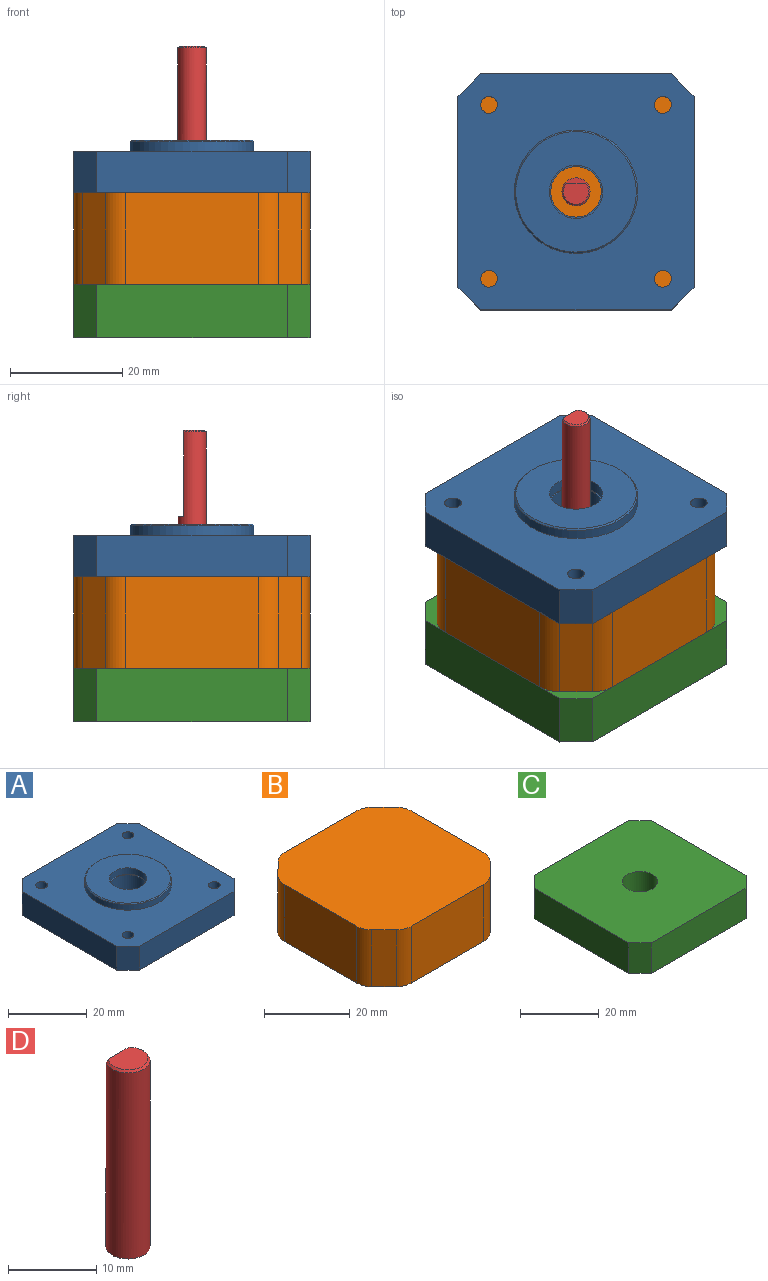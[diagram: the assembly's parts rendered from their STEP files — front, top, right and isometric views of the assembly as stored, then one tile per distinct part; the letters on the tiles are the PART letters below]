
ASSEMBLY  parts=4 mates=3
PART A: 20 faces, bbox 42.1x42.1x9.4 mm
  f0: plane 9.5x9.5mm, normal (0,0,1), area 7.3mm2, adj f11,f16
  f1: plane 34x7.4mm, normal (0,1,0), area 251.6mm2, adj f2,f12,f14,f15
  f2: plane 7.4x4.05mm, normal (-0.71,0.71,0), area 42.4mm2, adj f1,f3,f14,f15
  f3: plane 34x7.4mm, normal (-1,0,0), area 251.6mm2, adj f2,f4,f14,f15
  f4: plane 7.4x4.05mm, normal (-0.71,-0.71,0), area 42.4mm2, adj f3,f5,f14,f15
  f5: plane 34x7.4mm, normal (0,-1,0), area 251.6mm2, adj f4,f6,f14,f15
  f6: plane 7.4x4.05mm, normal (0.71,-0.71,0), area 42.4mm2, adj f5,f7,f14,f15
  f7: plane 34x7.4mm, normal (1,0,0), area 251.6mm2, adj f6,f12,f14,f15
  f8: cylinder r=1.5mm len=7.4mm, axis (0,0,-1), area 69.7mm2, adj f14,f15
  f9: cylinder r=1.5mm len=7.4mm, axis (0,0,-1), area 69.7mm2, adj f14,f15
  f10: cylinder r=1.5mm len=7.4mm, axis (0,0,-1), area 69.7mm2, adj f14,f15
  f11: cylinder r=4.5mm len=9mm, axis (0,0,-1), area 209.2mm2, adj f0,f15
  f12: plane 7.4x4.05mm, normal (0.71,0.71,0), area 42.4mm2, adj f1,f7,f14,f15
  f13: cylinder r=1.5mm len=7.4mm, axis (0,0,-1), area 69.7mm2, adj f14,f15
  f14: plane 42.1x42.1mm, normal (0,0,1), area 1331.2mm2, adj f1,f2,f3,f4,f5,f6,f7,f8
  f15: plane 42.1x42.1mm, normal (0,0,-1), area 1647.7mm2, adj f1,f2,f3,f4,f5,f6,f7,f8
  f16: cylinder r=4.75mm len=9.5mm, axis (0,0,-1), area 59.7mm2, adj f0,f18
  f17: cylinder r=11mm len=22mm, axis (0,0,-1), area 121mm2, adj f14,f19
  f18: plane 21.5x21.5mm, normal (0,0,1), area 292.2mm2, adj f16,f19
  f19: cone r=10.75mm half-angle=45deg, axis (0,0,-1), area 24.2mm2, adj f17,f18
PART B: 18 faces, bbox 42.1x42.1x16.3 mm
  f0: plane 16.3x4.12mm, normal (-0.71,0.71,0), area 95mm2, adj f8,f9,f10,f17
  f1: plane 23.86x16.3mm, normal (-1,0,0), area 388.9mm2, adj f8,f9,f10,f11
  f2: plane 16.3x4.12mm, normal (-0.71,-0.71,0), area 95mm2, adj f8,f9,f11,f12
  f3: plane 23.86x16.3mm, normal (0,-1,0), area 388.9mm2, adj f8,f9,f12,f13
  f4: plane 16.3x4.12mm, normal (0.71,-0.71,0), area 95mm2, adj f8,f9,f13,f14
  f5: plane 23.86x16.3mm, normal (1,0,0), area 388.9mm2, adj f8,f9,f14,f15
  f6: plane 16.3x4.12mm, normal (0.71,0.71,0), area 95mm2, adj f8,f9,f15,f16
  f7: plane 23.86x16.3mm, normal (0,1,0), area 388.9mm2, adj f8,f9,f16,f17
  f8: plane 42.1x42.1mm, normal (0,0,1), area 1668.7mm2, adj f0,f1,f2,f3,f4,f5,f6,f7
  f9: plane 42.1x42.1mm, normal (0,0,-1), area 1668.7mm2, adj f0,f1,f2,f3,f4,f5,f6,f7
  f10: cylinder r=5mm len=16.3mm, axis (0,0,1), area 64mm2, adj f0,f1,f8,f9
  f11: cylinder r=5mm len=16.3mm, axis (0,0,-1), area 64mm2, adj f1,f2,f8,f9
  f12: cylinder r=5mm len=16.3mm, axis (0,0,1), area 64mm2, adj f2,f3,f8,f9
  f13: cylinder r=5mm len=16.3mm, axis (0,0,-1), area 64mm2, adj f3,f4,f8,f9
  f14: cylinder r=5mm len=16.3mm, axis (0,0,1), area 64mm2, adj f4,f5,f8,f9
  f15: cylinder r=5mm len=16.3mm, axis (0,0,-1), area 64mm2, adj f5,f6,f8,f9
  f16: cylinder r=5mm len=16.3mm, axis (0,0,1), area 64mm2, adj f6,f7,f8,f9
  f17: cylinder r=5mm len=16.3mm, axis (0,0,-1), area 64mm2, adj f0,f7,f8,f9
PART C: 11 faces, bbox 42.1x42.1x9.5 mm
  f0: plane 34x9.5mm, normal (0,1,0), area 323mm2, adj f1,f8,f9,f10
  f1: plane 9.5x4.05mm, normal (-0.71,0.71,0), area 54.4mm2, adj f0,f2,f9,f10
  f2: plane 34x9.5mm, normal (-1,0,0), area 323mm2, adj f1,f3,f9,f10
  f3: plane 9.5x4.05mm, normal (-0.71,-0.71,0), area 54.4mm2, adj f2,f4,f9,f10
  f4: plane 34x9.5mm, normal (0,-1,0), area 323mm2, adj f3,f5,f9,f10
  f5: plane 9.5x4.05mm, normal (0.71,-0.71,0), area 54.4mm2, adj f4,f6,f9,f10
  f6: plane 34x9.5mm, normal (1,0,0), area 323mm2, adj f5,f8,f9,f10
  f7: cylinder r=4.5mm len=9.5mm, axis (0,0,-1), area 268.6mm2, adj f9,f10
  f8: plane 9.5x4.05mm, normal (0.71,0.71,0), area 54.4mm2, adj f0,f6,f9,f10
  f9: plane 42.1x42.1mm, normal (0,0,1), area 1676mm2, adj f0,f1,f2,f3,f4,f5,f6,f7
  f10: plane 42.1x42.1mm, normal (0,0,-1), area 1676mm2, adj f0,f1,f2,f3,f4,f5,f6,f7
PART D: 6 faces, bbox 5x5x26.1 mm
  f0: cylinder r=2.5mm len=25.85mm, axis (0,0,-1), area 336.3mm2, adj f2,f3,f4,f5
  f1: plane 4.5x3.75mm, normal (0,0,1), area 14.2mm2, adj f3,f5
  f2: plane 5x5mm, normal (0,0,-1), area 19.6mm2, adj f0
  f3: cone r=2.25mm half-angle=45deg, axis (0,0,-1), area 3.8mm2, adj f0,f1,f5
  f4: plane 4x1mm, normal (0,0,1), area 2.8mm2, adj f0,f5
  f5: plane 15.31x4.01mm, normal (0,1,0), area 61.1mm2, adj f0,f1,f3,f4
PLACE A t=(62.81,67.34,44.55)mm
PLACE B t=(62.81,67.34,44.55)mm
PLACE C t=(62.81,67.34,44.55)mm
PLACE D t=(62.81,67.34,44.55)mm
MATE fastened B.f9 <-> C.f7  axis (0,0,-1) through (62.81,67.34,54.05)mm
MATE fastened A.f11 <-> B.f8  axis (0,0,-1) through (62.81,67.34,70.35)mm
MATE fastened B.f8 <-> D.f0  axis (0,0,1) through (62.81,67.34,70.35)mm
